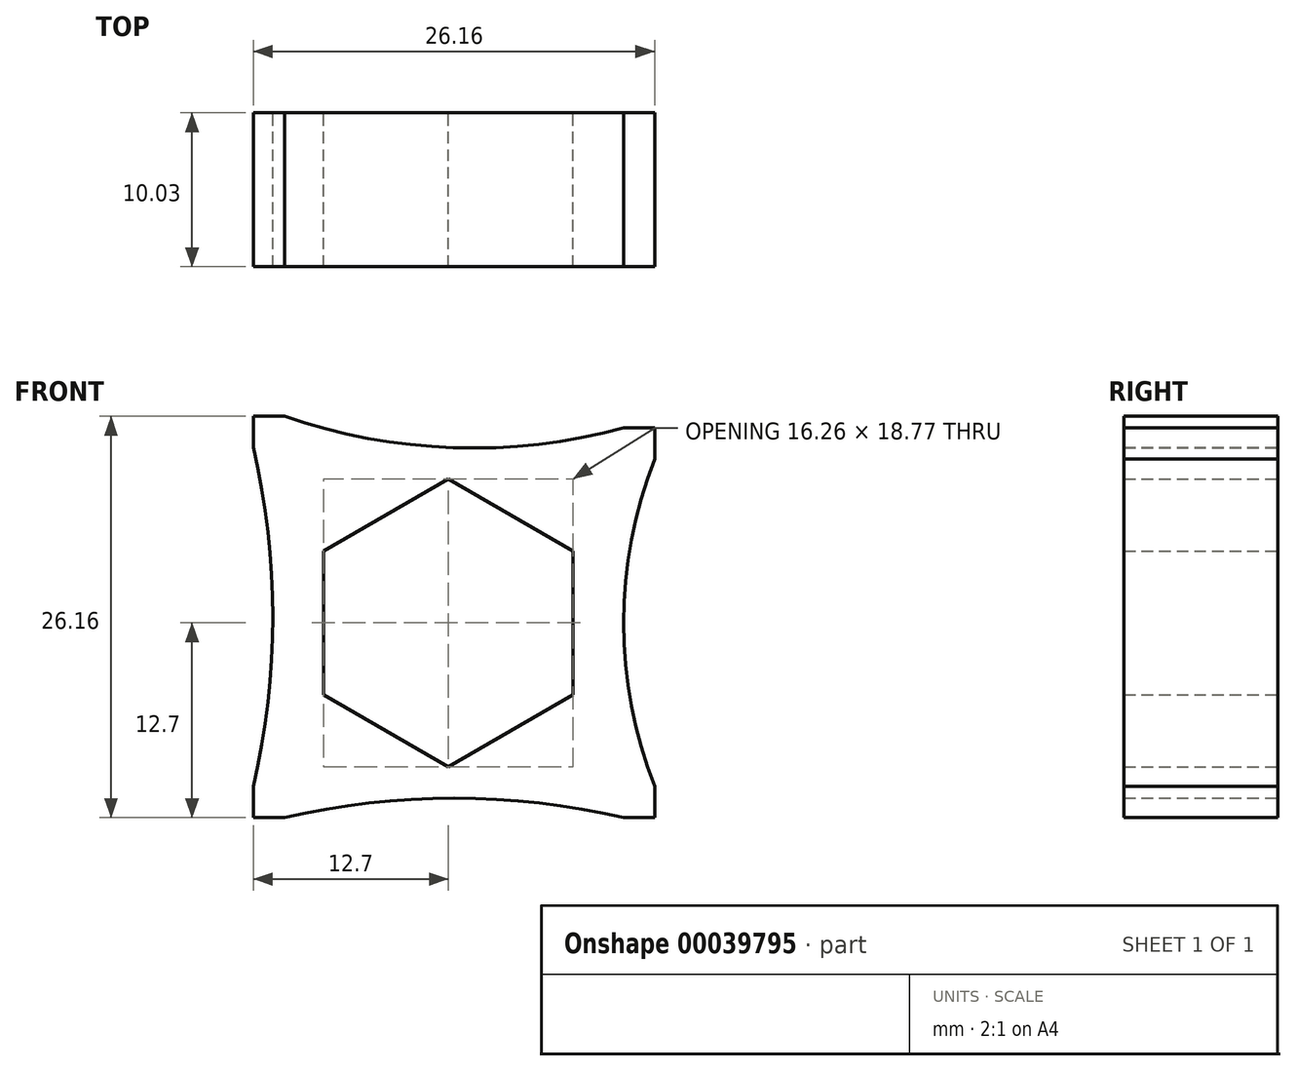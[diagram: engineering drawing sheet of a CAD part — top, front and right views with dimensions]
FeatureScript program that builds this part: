
annotation { "Feature Type Name" : "Feature", "Feature Type Description" : "" }
export const myFeature = defineFeature(function(context is Context, id is Id, definition is map)
    precondition{}
    {
        {
            var Q0;
            Q0=qCreatedBy(makeId("Front.planeOp"),FACE);
            var sketch = newSketch(context, id + "F0", { "sketchPlane" : qUnion([Q0])});
            skLineSegment(sketch, "E0", {"start": v(0, 0) * mm, "end": v(8.13, 0) * mm});
            skCircle(sketch, "E1.cCircle", {"center": v(0, 0) * mm, "radius": 8.13 * mm, "construction": true});
            skLineSegment(sketch, "E1.0", {"start": v(8.13, 4.7) * mm, "end": v(8.13, -4.7) * mm});
            skLineSegment(sketch, "E1.1", {"start": v(8.13, -4.7) * mm, "end": v(0, -9.39) * mm});
            skLineSegment(sketch, "E1.2", {"start": v(0, -9.39) * mm, "end": v(-8.13, -4.7) * mm});
            skLineSegment(sketch, "E1.3", {"start": v(-8.13, -4.7) * mm, "end": v(-8.13, 4.7) * mm});
            skLineSegment(sketch, "E1.4", {"start": v(-8.13, 4.7) * mm, "end": v(0, 9.39) * mm});
            skLineSegment(sketch, "E1.5", {"start": v(0, 9.39) * mm, "end": v(8.13, 4.7) * mm});
            skPoint(sketch, "E1.0.midPoint", {"position": v(8.13, 0) * mm});
            skLineSegment(sketch, "E2", {"start": v(0, 0) * mm, "end": v(12.7, 0) * mm});
            skLineSegment(sketch, "E3", {"start": v(0, 0) * mm, "end": v(-12.7, 0) * mm});
            skLineSegment(sketch, "E4", {"start": v(12.7, 0) * mm, "end": v(11.43, 0) * mm});
            skLineSegment(sketch, "E5", {"start": v(-12.7, 0) * mm, "end": v(-10.16, 0) * mm});
            skLineSegment(sketch, "E6", {"start": v(-12.7, 0) * mm, "end": v(-11.43, 0) * mm});
            skLineSegment(sketch, "E7", {"start": v(-12.7, 13.46) * mm, "end": v(-12.7, 11.43) * mm});
            skLineSegment(sketch, "E8", {"start": v(-12.7, -12.7) * mm, "end": v(-12.7, -10.67) * mm});
            skLineSegment(sketch, "E9", {"start": v(-12.7, 13.46) * mm, "end": v(-10.67, 13.46) * mm});
            skLineSegment(sketch, "E10", {"start": v(13.46, 12.7) * mm, "end": v(11.43, 12.7) * mm});
            skLineSegment(sketch, "E11", {"start": v(0, 12.7) * mm, "end": v(0, 11.43) * mm});
            skLineSegment(sketch, "E12", {"start": v(-12.7, -12.7) * mm, "end": v(-10.67, -12.7) * mm});
            skLineSegment(sketch, "E13", {"start": v(13.46, -12.7) * mm, "end": v(13.46, -10.67) * mm});
            skLineSegment(sketch, "E14", {"start": v(13.46, -12.7) * mm, "end": v(13.46, -11.68) * mm});
            skLineSegment(sketch, "E15", {"start": v(13.46, 12.7) * mm, "end": v(13.46, 10.67) * mm});
            skLineSegment(sketch, "E16", {"start": v(13.46, 12.7) * mm, "end": v(13.46, 11.68) * mm});
            skLineSegment(sketch, "E17", {"start": v(13.46, -12.7) * mm, "end": v(11.43, -12.7) * mm});
            skLineSegment(sketch, "E18", {"start": v(0, -12.7) * mm, "end": v(0, -11.43) * mm});
            skPoint(sketch, "E18.endSnap0", {"position": v(0, -12.7) * mm});
            skArc(sketch, "E19", {"start": v(-10.67, 13.46) * mm, "mid": v(0.32, 11.42) * mm, "end": v(11.43, 12.7) * mm});
            skArc(sketch, "E20", {"start": v(-12.7, -10.67) * mm, "mid": v(-11.43, 0.38) * mm, "end": v(-12.7, 11.43) * mm});
            skArc(sketch, "E21", {"start": v(11.43, -12.7) * mm, "mid": v(0.38, -11.43) * mm, "end": v(-10.67, -12.7) * mm});
            skArc(sketch, "E22", {"start": v(13.46, 10.67) * mm, "mid": v(11.43, 0) * mm, "end": v(13.46, -10.67) * mm});
            skSolve(sketch);
        }
        {
            var Q0;
            Q0=qSketchRegion(id+"F0",true);
            extrude(context, id + "F1", {"entities" : qUnion([Q0]), "depth" : 10.03 * mm});
        }
    });
